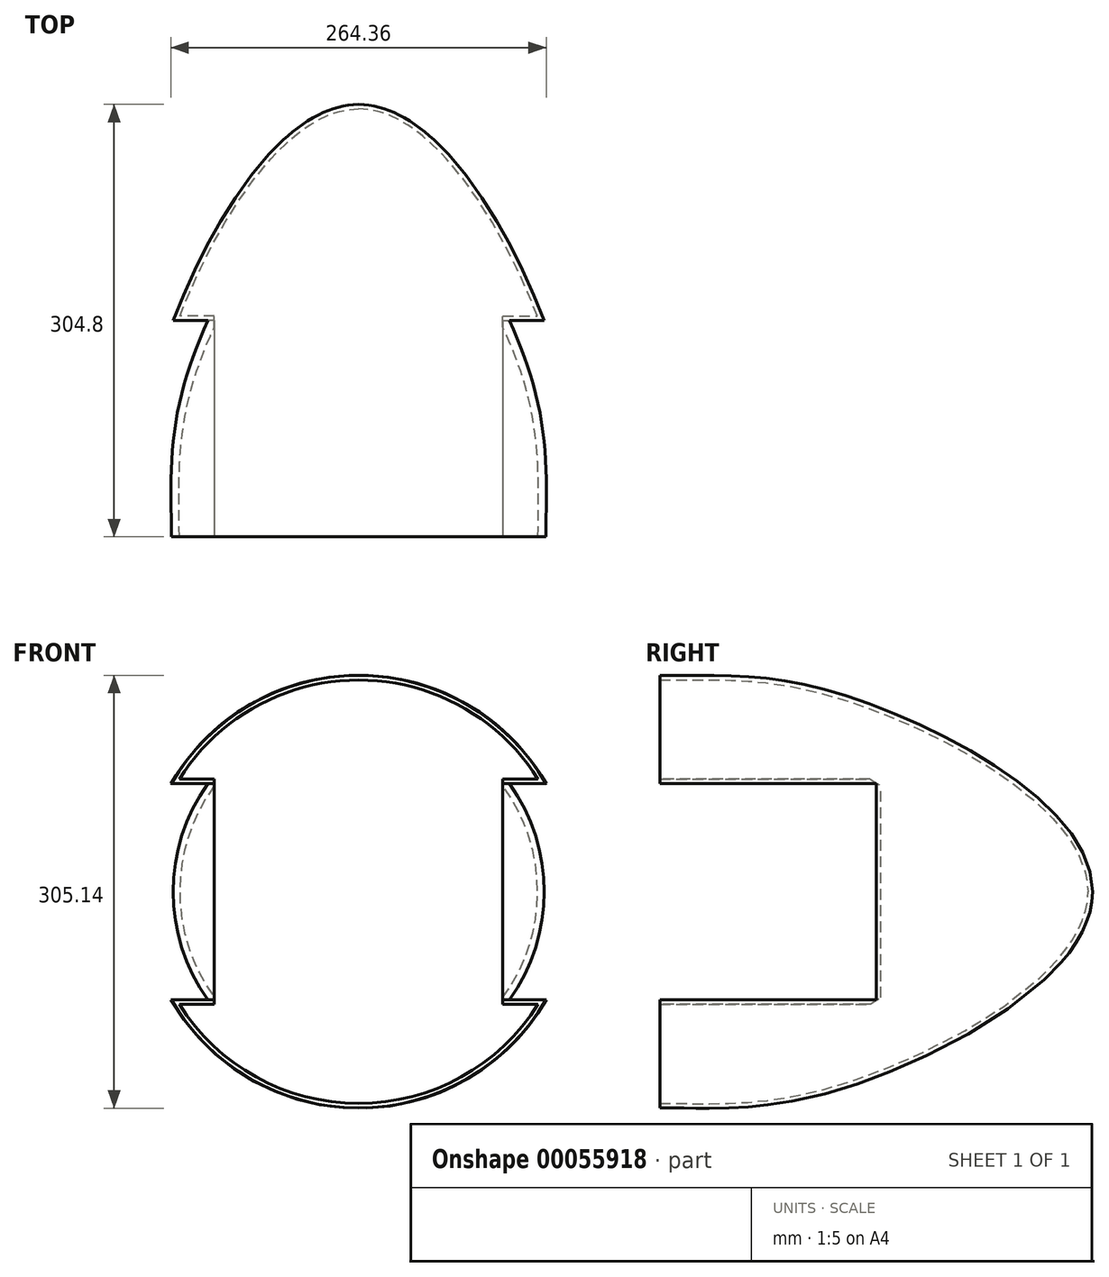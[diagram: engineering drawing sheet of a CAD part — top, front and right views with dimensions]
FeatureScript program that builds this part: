
annotation { "Feature Type Name" : "Feature", "Feature Type Description" : "" }
export const myFeature = defineFeature(function(context is Context, id is Id, definition is map)
    precondition{}
    {
        {
            var Q0;
            Q0=qCreatedBy(makeId("Right.planeOp"),FACE);
            var sketch = newSketch(context, id + "F0", { "sketchPlane" : qUnion([Q0])});
            skLineSegment(sketch, "E0", {"start": v(0, 0) * mm, "end": v(304.8, 0) * mm});
            skLineSegment(sketch, "E1", {"start": v(0, 0) * mm, "end": v(0, 152.4) * mm});
            skFitSpline(sketch, "E2", {"points": [v(0, 152.4) * mm, v(132.04, 137.77) * mm, v(304.8, 0) * mm], "startDerivative": vector(310.81, 0.55) * mm, "endDerivative": vector(0.83, -323.18) * mm});
            skSolve(sketch);
        }
        {
            var Q0;
            Q0=makeQuery(id+"F0.imprint","IMPRINT",FACE,{"disambiguationData":[TD([[makeQuery(id+"F0.imprint","IMPRINT",EDGE,{"derivedFrom":sQuery(id+"F0.wireOp",EDGE,"E0")}),1.0]])]});
            var Q1;
            Q1=sQuery(id+"F0.wireOp",EDGE,"E0");
            revolve(context, id + "F1", {"entities" : qUnion([Q0]), "axis" : qUnion([Q1]), "revolveType" : RevolveType.FULL});
        }
        {
            var Q0;
            Q0=makeQuery(id+"F1.opRevolve","SWEPT_FACE",FACE,{"disambiguationData":[OSD([sQuery(id+"F0.wireOp",EDGE,"E1")])]});
            var sketch = newSketch(context, id + "F2", { "sketchPlane" : qUnion([Q0])});
            skLineSegment(sketch, "E3", {"start": v(0, 0) * mm, "end": v(101.6, 0) * mm});
            skLineSegment(sketch, "E4", {"start": v(101.6, 0) * mm, "end": v(101.6, 76.2) * mm});
            skLineSegment(sketch, "E5", {"start": v(0, 0) * mm, "end": v(0, 100.24) * mm});
            skLineSegment(sketch, "E6.bottom", {"start": v(101.6, 76.2) * mm, "end": v(166.1, 76.2) * mm});
            skLineSegment(sketch, "E6.top", {"start": v(101.6, -76.2) * mm, "end": v(166.1, -76.2) * mm});
            skLineSegment(sketch, "E6.left", {"start": v(101.6, 76.2) * mm, "end": v(101.6, -76.2) * mm});
            skLineSegment(sketch, "E6.right", {"start": v(166.1, 76.2) * mm, "end": v(166.1, -76.2) * mm});
            skLineSegment(sketch, "E7", {"start": v(0, 0) * mm, "end": v(-101.6, 0) * mm});
            skLineSegment(sketch, "E8", {"start": v(-101.6, 0) * mm, "end": v(-101.6, 76.2) * mm});
            skLineSegment(sketch, "E9.bottom", {"start": v(-101.6, 76.2) * mm, "end": v(-174.5, 76.2) * mm});
            skLineSegment(sketch, "E9.top", {"start": v(-101.6, -76.2) * mm, "end": v(-174.5, -76.2) * mm});
            skLineSegment(sketch, "E9.left", {"start": v(-101.6, 76.2) * mm, "end": v(-101.6, -76.2) * mm});
            skLineSegment(sketch, "E9.right", {"start": v(-174.5, 76.2) * mm, "end": v(-174.5, -76.2) * mm});
            skSolve(sketch);
        }
        {
            var Q0;
            Q0 = qSketchRegion(id + "F2", true);
            extrude(context, id + "F3", {"entities" : qUnion([Q0]), "operationType" : NewBodyOperationType.REMOVE, "oppositeDirection" : true, "depth" : 152.4 * mm});
        }
        {
            var Q0;
            Q0=makeQuery(id+"F1.opRevolve","SWEPT_FACE",FACE,{"disambiguationData":[OSD([sQuery(id+"F0.wireOp",EDGE,"E1")])]});
            var Q1;
            Q1=makeQuery(id+"F3.boolean.opBoolean","COPY",FACE,{"derivedFrom":makeQuery(id+"F3.opExtrude","SWEPT_FACE",FACE,{"disambiguationData":[OSD([sQuery(id+"F2.wireOp",EDGE,"E9.left")])]})});
            var Q2;
            Q2=makeQuery(id+"F3.boolean.opBoolean","COPY",FACE,{"derivedFrom":makeQuery(id+"F3.opExtrude","SWEPT_FACE",FACE,{"disambiguationData":[OSD([sQuery(id+"F2.wireOp",EDGE,"E6.left")])]})});
            shell(context, id + "F4", {"entities" : qUnion([Q0, Q1, Q2]), "thickness" : 3.17 * mm});
        }
    });
